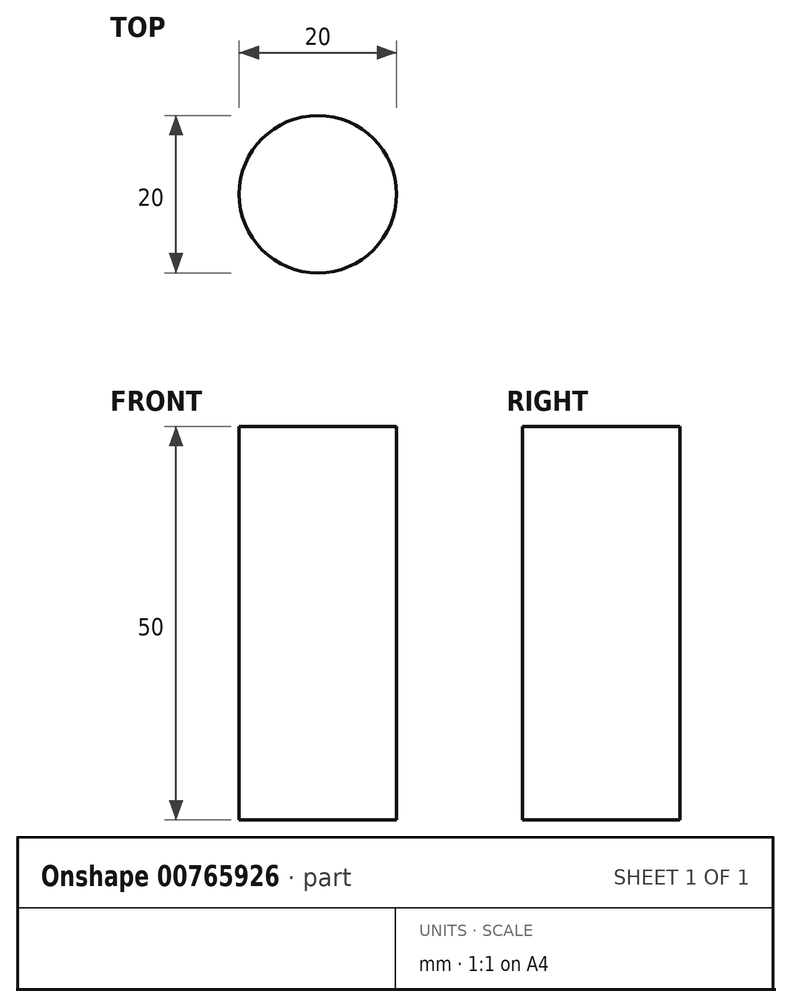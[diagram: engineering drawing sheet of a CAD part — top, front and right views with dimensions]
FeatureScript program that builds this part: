
annotation { "Feature Type Name" : "Feature", "Feature Type Description" : "" }
export const myFeature = defineFeature(function(context is Context, id is Id, definition is map)
    precondition{}
    {
        {
            assignVariable(context, id + "F0", {"name" : "Height", "anyValue" : 50});
        }
        {
            var Q0;
            Q0=qCreatedBy(makeId("Top.planeOp"),FACE);
            var sketch = newSketch(context, id + "F1", { "sketchPlane" : qUnion([Q0])});
            skCircle(sketch, "E0", {"center": v(0, 0) * mm, "radius": 10 * mm});
            skSolve(sketch);
        }
        {
            var Q0;
            Q0=makeQuery(id+"F1.imprint","IMPRINT",FACE,{"disambiguationData":[TD([[makeQuery(id+"F1.imprint","IMPRINT",EDGE,{"derivedFrom":sQuery(id+"F1.wireOp",EDGE,"E0")}),1.0]])]});
            extrude(context, id + "F2", {"entities" : qUnion([Q0]), "depth" : (getVariable(context, 'Height')) * mm, "offsetDistance" : 25 * mm});
        }
    });
